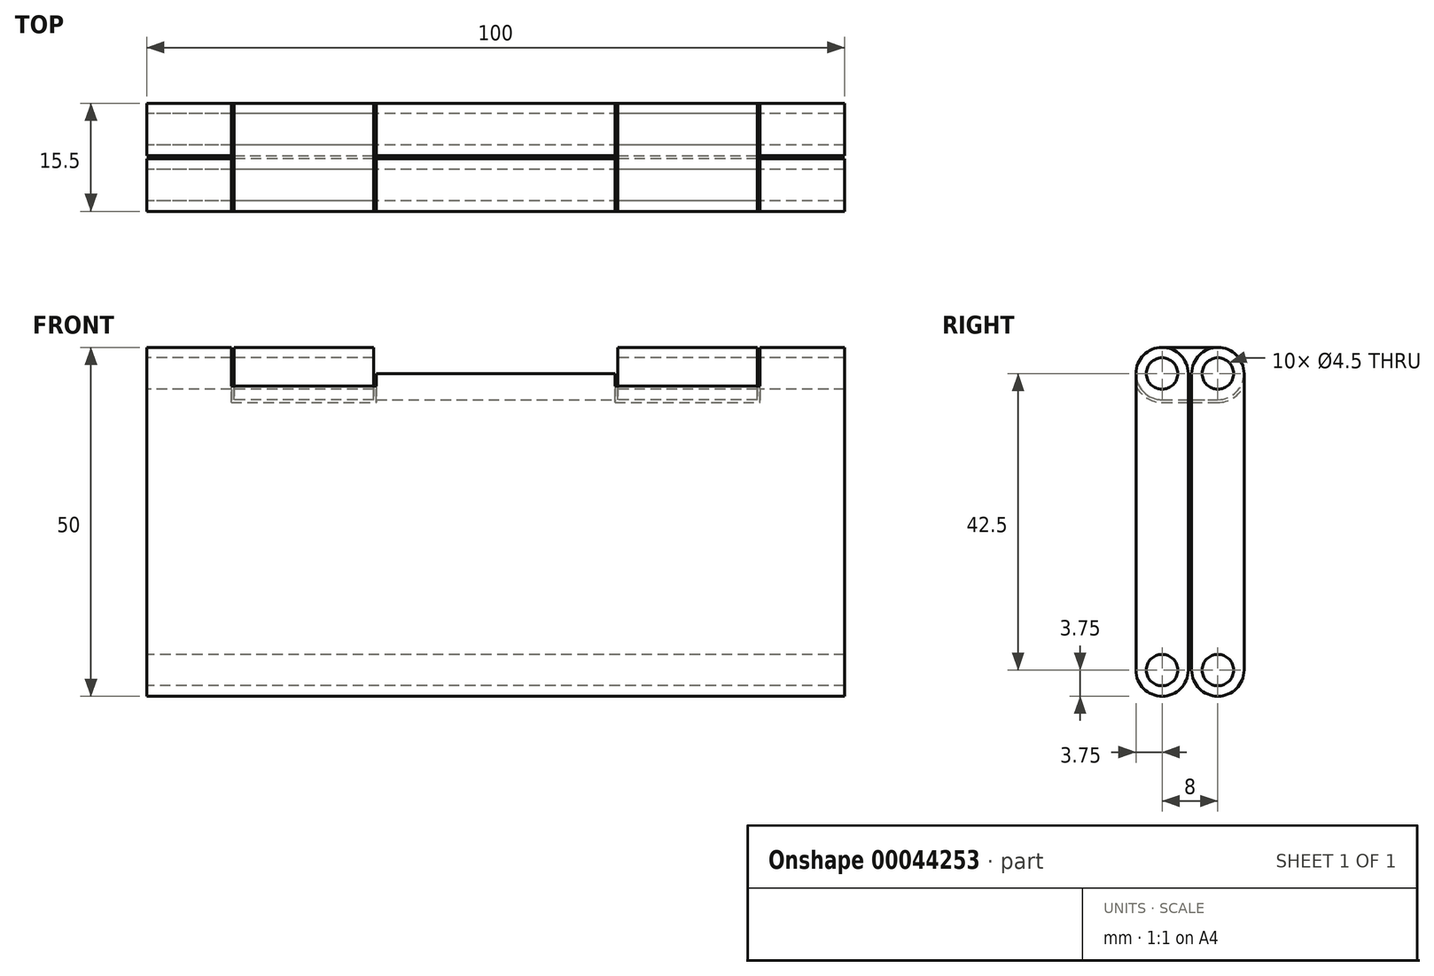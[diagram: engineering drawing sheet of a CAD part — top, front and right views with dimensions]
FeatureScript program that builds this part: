
annotation { "Feature Type Name" : "Feature", "Feature Type Description" : "" }
export const myFeature = defineFeature(function(context is Context, id is Id, definition is map)
    precondition{}
    {
        {
            var Q0;
            Q0=qCreatedBy(makeId("Right.planeOp"),FACE);
            var sketch = newSketch(context, id + "F0", { "sketchPlane" : qUnion([Q0])});
            skLineSegment(sketch, "E0.bottom", {"start": v(0, 0) * mm, "end": v(7.5, 0) * mm});
            skLineSegment(sketch, "E0.top", {"start": v(0, 50) * mm, "end": v(7.5, 50) * mm});
            skLineSegment(sketch, "E0.left", {"start": v(0, 0) * mm, "end": v(0, 50) * mm});
            skLineSegment(sketch, "E0.right", {"start": v(7.5, 0) * mm, "end": v(7.5, 50) * mm});
            skCircle(sketch, "E1", {"center": v(3.75, 3.75) * mm, "radius": 3.75 * mm});
            skPoint(sketch, "E1.centerSnap0", {"position": v(3.75, 0) * mm});
            skCircle(sketch, "E2", {"center": v(3.75, 3.75) * mm, "radius": 2.25 * mm});
            skCircle(sketch, "E3", {"center": v(3.75, 46.25) * mm, "radius": 3.75 * mm});
            skCircle(sketch, "E4", {"center": v(3.75, 46.25) * mm, "radius": 2.25 * mm});
            skLineSegment(sketch, "E5", {"start": v(3.75, 50) * mm, "end": v(11.75, 50) * mm});
            skLineSegment(sketch, "E6", {"start": v(3.75, 42.5) * mm, "end": v(11.75, 42.5) * mm});
            skCircle(sketch, "E7", {"center": v(11.75, 46.25) * mm, "radius": 3.75 * mm});
            skCircle(sketch, "E8", {"center": v(11.75, 46.25) * mm, "radius": 2.25 * mm});
            skLineSegment(sketch, "E9", {"start": v(8, 46.25) * mm, "end": v(8, 3.75) * mm});
            skLineSegment(sketch, "E10", {"start": v(15.5, 46.25) * mm, "end": v(15.5, 3.75) * mm});
            skCircle(sketch, "E11", {"center": v(11.75, 3.75) * mm, "radius": 3.75 * mm});
            skCircle(sketch, "E12", {"center": v(11.75, 3.75) * mm, "radius": 2.25 * mm});
            skLineSegment(sketch, "E13", {"start": v(3.75, 7.5) * mm, "end": v(11.75, 7.5) * mm});
            skLineSegment(sketch, "E14", {"start": v(11.75, 0) * mm, "end": v(3.75, 0) * mm});
            skLineSegment(sketch, "E15", {"start": v(11.75, 7.5) * mm, "end": v(19.75, 7.5) * mm});
            skLineSegment(sketch, "E16", {"start": v(11.75, 0) * mm, "end": v(19.75, 0) * mm});
            skCircle(sketch, "E17", {"center": v(19.75, 3.75) * mm, "radius": 3.75 * mm});
            skCircle(sketch, "E18", {"center": v(19.75, 3.75) * mm, "radius": 2.25 * mm});
            skSolve(sketch);
        }
        {
            var Q0;
            {var subQ1=sQuery(id+"F0.wireOp",EDGE,"E1");var subQ3=sQuery(id+"F0.wireOp",EDGE,"E0.left");var subQ4=makeQuery(id+"F0.imprint","INTERSECT",VERTEX,{"derivedFrom":[subQ3,subQ1]});Q0=makeQuery(id+"F0.imprint","IMPRINT",FACE,{"disambiguationData":[TD([[makeQuery(id+"F0.imprint","IMPRINT",EDGE,{"disambiguationData":[TD([[subQ4,-1.0]])],"derivedFrom":subQ3}),-1.0]])]});}
            var Q1;
            Q1=makeQuery(id+"F0.imprint","IMPRINT",FACE,{"disambiguationData":[TD([[makeQuery(id+"F0.imprint","IMPRINT",EDGE,{"derivedFrom":sQuery(id+"F0.wireOp",EDGE,"E2")}),-1.0]])]});
            var Q2;
            {var subQ0=sQuery(id+"F0.wireOp",EDGE,"E1");var subQ1=sQuery(id+"F0.wireOp",EDGE,"E0.right");var subQ2=makeQuery(id+"F0.imprint","INTERSECT",VERTEX,{"derivedFrom":[subQ1,subQ0]});Q2=makeQuery(id+"F0.imprint","IMPRINT",FACE,{"disambiguationData":[TD([[makeQuery(id+"F0.imprint","IMPRINT",EDGE,{"disambiguationData":[TD([[subQ2,-1.0]])],"derivedFrom":subQ1}),1.0]])]});}
            var Q3;
            {var subQ0=sQuery(id+"F0.wireOp",EDGE,"E6");var subQ1=sQuery(id+"F0.wireOp",EDGE,"E0.right");var subQ2=makeQuery(id+"F0.imprint","INTERSECT",VERTEX,{"derivedFrom":[subQ1,subQ0]});Q3=makeQuery(id+"F0.imprint","IMPRINT",FACE,{"disambiguationData":[TD([[makeQuery(id+"F0.imprint","IMPRINT",EDGE,{"disambiguationData":[TD([[subQ2,-1.0]])],"derivedFrom":subQ1}),1.0]])]});}
            var Q4;
            Q4=makeQuery(id+"F0.imprint","IMPRINT",FACE,{"disambiguationData":[TD([[makeQuery(id+"F0.imprint","IMPRINT",EDGE,{"derivedFrom":sQuery(id+"F0.wireOp",EDGE,"E4")}),-1.0]])]});
            var Q5;
            Q5=makeQuery(id+"F0.imprint","IMPRINT",FACE,{"disambiguationData":[TD([[makeQuery(id+"F0.imprint","IMPRINT",EDGE,{"derivedFrom":sQuery(id+"F0.wireOp",EDGE,"E8")}),-1.0]])]});
            var Q6;
            {var subQ0=sQuery(id+"F0.wireOp",EDGE,"E7");var subQ1=sQuery(id+"F0.wireOp",EDGE,"E6");var subQ2=makeQuery(id+"F0.imprint","INTERSECT",VERTEX,{"derivedFrom":[subQ1,subQ0]});Q6=makeQuery(id+"F0.imprint","IMPRINT",FACE,{"disambiguationData":[TD([[makeQuery(id+"F0.imprint","IMPRINT",EDGE,{"disambiguationData":[TD([[subQ2,1.0]])],"derivedFrom":subQ1}),1.0]])]});}
            var Q7;
            {var subQ5=sQuery(id+"F0.wireOp",EDGE,"E10");Q7=makeQuery(id+"F0.imprint","IMPRINT",FACE,{"disambiguationData":[TD([[makeQuery(id+"F0.imprint","IMPRINT",EDGE,{"derivedFrom":subQ5}),-1.0]])]});}
            var Q8;
            {var subQ0=sQuery(id+"F0.wireOp",EDGE,"E11");var subQ1=sQuery(id+"F0.wireOp",EDGE,"E9");var subQ2=makeQuery(id+"F0.imprint","INTERSECT",VERTEX,{"derivedFrom":[subQ1,subQ0]});Q8=makeQuery(id+"F0.imprint","IMPRINT",FACE,{"disambiguationData":[TD([[makeQuery(id+"F0.imprint","IMPRINT",EDGE,{"disambiguationData":[TD([[subQ2,1.0]])],"derivedFrom":subQ1}),1.0]])]});}
            var Q9;
            Q9=makeQuery(id+"F0.imprint","IMPRINT",FACE,{"disambiguationData":[TD([[makeQuery(id+"F0.imprint","IMPRINT",EDGE,{"derivedFrom":sQuery(id+"F0.wireOp",EDGE,"E12")}),-1.0]])]});
            var Q10;
            {var subQ1=sQuery(id+"F0.wireOp",EDGE,"E6");var subQ8=sQuery(id+"F0.wireOp",EDGE,"E7");var subQ11=makeQuery(id+"F0.imprint","INTERSECT",VERTEX,{"derivedFrom":[subQ1,subQ8]});Q10=makeQuery(id+"F0.imprint","IMPRINT",FACE,{"disambiguationData":[TD([[makeQuery(id+"F0.imprint","IMPRINT",EDGE,{"disambiguationData":[TD([[subQ11,1.0]])],"derivedFrom":subQ1}),-1.0]])]});}
            extrude(context, id + "F1", {"entities" : qUnion([Q0, Q1, Q2, Q3, Q4, Q5, Q6, Q7, Q8, Q9, Q10]), "endBound" : BoundingType.SYMMETRIC, "depth" : 100 * mm, "offsetDistance" : 25 * mm});
        }
        {
            var Q0;
            Q0=makeQuery(id+"F0.imprint","IMPRINT",FACE,{"disambiguationData":[TD([[makeQuery(id+"F0.imprint","IMPRINT",EDGE,{"derivedFrom":sQuery(id+"F0.wireOp",EDGE,"E4")}),-1.0]])]});
            var Q1;
            {var subQ0=sQuery(id+"F0.wireOp",EDGE,"E6");var subQ1=sQuery(id+"F0.wireOp",EDGE,"E0.right");var subQ2=makeQuery(id+"F0.imprint","INTERSECT",VERTEX,{"derivedFrom":[subQ1,subQ0]});Q1=makeQuery(id+"F0.imprint","IMPRINT",FACE,{"disambiguationData":[TD([[makeQuery(id+"F0.imprint","IMPRINT",EDGE,{"disambiguationData":[TD([[subQ2,-1.0]])],"derivedFrom":subQ1}),1.0]])]});}
            var Q2;
            {var subQ1=sQuery(id+"F0.wireOp",EDGE,"E0.right");var subQ6=sQuery(id+"F0.wireOp",EDGE,"E6");var subQ7=makeQuery(id+"F0.imprint","INTERSECT",VERTEX,{"derivedFrom":[subQ1,subQ6]});Q2=makeQuery(id+"F0.imprint","IMPRINT",FACE,{"disambiguationData":[TD([[makeQuery(id+"F0.imprint","IMPRINT",EDGE,{"disambiguationData":[TD([[subQ7,-1.0]])],"derivedFrom":subQ1}),-1.0]])]});}
            var Q3;
            {var subQ0=sQuery(id+"F0.wireOp",EDGE,"E7");var subQ1=sQuery(id+"F0.wireOp",EDGE,"E6");var subQ2=makeQuery(id+"F0.imprint","INTERSECT",VERTEX,{"derivedFrom":[subQ1,subQ0]});Q3=makeQuery(id+"F0.imprint","IMPRINT",FACE,{"disambiguationData":[TD([[makeQuery(id+"F0.imprint","IMPRINT",EDGE,{"disambiguationData":[TD([[subQ2,1.0]])],"derivedFrom":subQ1}),1.0]])]});}
            var Q4;
            {var subQ0=sQuery(id+"F0.wireOp",EDGE,"E5");var subQ1=sQuery(id+"F0.wireOp",EDGE,"E0.right");var subQ2=makeQuery(id+"F0.imprint","INTERSECT",VERTEX,{"derivedFrom":[subQ1,subQ0]});Q4=makeQuery(id+"F0.imprint","IMPRINT",FACE,{"disambiguationData":[TD([[makeQuery(id+"F0.imprint","IMPRINT",EDGE,{"disambiguationData":[TD([[subQ2,1.0]])],"derivedFrom":subQ1}),1.0]])]});}
            var Q5;
            Q5=makeQuery(id+"F0.imprint","IMPRINT",FACE,{"disambiguationData":[TD([[makeQuery(id+"F0.imprint","IMPRINT",EDGE,{"derivedFrom":sQuery(id+"F0.wireOp",EDGE,"E8")}),-1.0]])]});
            extrude(context, id + "F2", {"entities" : qUnion([Q0, Q1, Q2, Q3, Q4, Q5]), "endBound" : BoundingType.SYMMETRIC, "depth" : 75 * mm, "offsetDistance" : 25 * mm});
        }
        {
            var Q0;
            Q0=makeQuery(id+"F0.imprint","IMPRINT",FACE,{"disambiguationData":[TD([[makeQuery(id+"F0.imprint","IMPRINT",EDGE,{"derivedFrom":sQuery(id+"F0.wireOp",EDGE,"E4")}),-1.0]])]});
            var Q1;
            {var subQ0=sQuery(id+"F0.wireOp",EDGE,"E5");var subQ1=sQuery(id+"F0.wireOp",EDGE,"E0.right");var subQ2=makeQuery(id+"F0.imprint","INTERSECT",VERTEX,{"derivedFrom":[subQ1,subQ0]});Q1=makeQuery(id+"F0.imprint","IMPRINT",FACE,{"disambiguationData":[TD([[makeQuery(id+"F0.imprint","IMPRINT",EDGE,{"disambiguationData":[TD([[subQ2,1.0]])],"derivedFrom":subQ1}),1.0]])]});}
            var Q2;
            {var subQ1=sQuery(id+"F0.wireOp",EDGE,"E0.right");var subQ6=sQuery(id+"F0.wireOp",EDGE,"E6");var subQ7=makeQuery(id+"F0.imprint","INTERSECT",VERTEX,{"derivedFrom":[subQ1,subQ6]});Q2=makeQuery(id+"F0.imprint","IMPRINT",FACE,{"disambiguationData":[TD([[makeQuery(id+"F0.imprint","IMPRINT",EDGE,{"disambiguationData":[TD([[subQ7,-1.0]])],"derivedFrom":subQ1}),-1.0]])]});}
            var Q3;
            Q3=makeQuery(id+"F0.imprint","IMPRINT",FACE,{"disambiguationData":[TD([[makeQuery(id+"F0.imprint","IMPRINT",EDGE,{"derivedFrom":sQuery(id+"F0.wireOp",EDGE,"E8")}),-1.0]])]});
            var Q4;
            {var subQ0=sQuery(id+"F0.wireOp",EDGE,"E7");var subQ1=sQuery(id+"F0.wireOp",EDGE,"E6");var subQ2=makeQuery(id+"F0.imprint","INTERSECT",VERTEX,{"derivedFrom":[subQ1,subQ0]});Q4=makeQuery(id+"F0.imprint","IMPRINT",FACE,{"disambiguationData":[TD([[makeQuery(id+"F0.imprint","IMPRINT",EDGE,{"disambiguationData":[TD([[subQ2,1.0]])],"derivedFrom":subQ1}),1.0]])]});}
            var Q5;
            {var subQ0=sQuery(id+"F0.wireOp",EDGE,"E6");var subQ1=sQuery(id+"F0.wireOp",EDGE,"E0.right");var subQ2=makeQuery(id+"F0.imprint","INTERSECT",VERTEX,{"derivedFrom":[subQ1,subQ0]});Q5=makeQuery(id+"F0.imprint","IMPRINT",FACE,{"disambiguationData":[TD([[makeQuery(id+"F0.imprint","IMPRINT",EDGE,{"disambiguationData":[TD([[subQ2,-1.0]])],"derivedFrom":subQ1}),1.0]])]});}
            extrude(context, id + "F3", {"entities" : qUnion([Q0, Q1, Q2, Q3, Q4, Q5]), "operationType" : NewBodyOperationType.REMOVE, "endBound" : BoundingType.SYMMETRIC, "depth" : 35 * mm, "offsetDistance" : 25 * mm});
        }
        {
            var Q0;
            Q0=makeQuery(id+"F3.boolean.opBoolean","SPLIT",BODY,{"disambiguationData":[OD(1.0)],"derivedFrom":makeQuery(id+"F2.opExtrude","SWEPT_BODY",BODY,{"disambiguationData":[OSD([sQuery(id+"F0.wireOp",EDGE,"E3"),sQuery(id+"F0.wireOp",EDGE,"E4"),sQuery(id+"F0.wireOp",EDGE,"E5"),sQuery(id+"F0.wireOp",EDGE,"E6"),sQuery(id+"F0.wireOp",EDGE,"E7"),sQuery(id+"F0.wireOp",EDGE,"E8")])]})});
            var Q1;
            Q1=makeQuery(id+"F3.boolean.opBoolean","SPLIT",BODY,{"disambiguationData":[OD(0.0)],"derivedFrom":makeQuery(id+"F2.opExtrude","SWEPT_BODY",BODY,{"disambiguationData":[OSD([sQuery(id+"F0.wireOp",EDGE,"E3"),sQuery(id+"F0.wireOp",EDGE,"E4"),sQuery(id+"F0.wireOp",EDGE,"E5"),sQuery(id+"F0.wireOp",EDGE,"E6"),sQuery(id+"F0.wireOp",EDGE,"E7"),sQuery(id+"F0.wireOp",EDGE,"E8")])]})});
            var Q2;
            Q2=makeQuery(id+"F1.opExtrude","SWEPT_BODY",BODY,{"disambiguationData":[OSD([sQuery(id+"F0.wireOp",EDGE,"E0.left"),sQuery(id+"F0.wireOp",EDGE,"E0.right"),sQuery(id+"F0.wireOp",EDGE,"E1"),sQuery(id+"F0.wireOp",EDGE,"E2"),sQuery(id+"F0.wireOp",EDGE,"E3"),sQuery(id+"F0.wireOp",EDGE,"E4")])]});
            var Q3;
            Q3=makeQuery(id+"F1.opExtrude","SWEPT_BODY",BODY,{"disambiguationData":[OSD([sQuery(id+"F0.wireOp",EDGE,"E7"),sQuery(id+"F0.wireOp",EDGE,"E8"),sQuery(id+"F0.wireOp",EDGE,"E9"),sQuery(id+"F0.wireOp",EDGE,"E10"),sQuery(id+"F0.wireOp",EDGE,"E11"),sQuery(id+"F0.wireOp",EDGE,"E12")])]});
            booleanBodies(context, id + "F4", {"operationType" : BooleanOperationType.SUBTRACTION, "tools" : qUnion([Q0, Q1]), "targets" : qUnion([Q2, Q3]), "offset" : true, "offsetAll" : true, "offsetDistance" : .4 * mm, "keepTools" : true});
        }
    });
